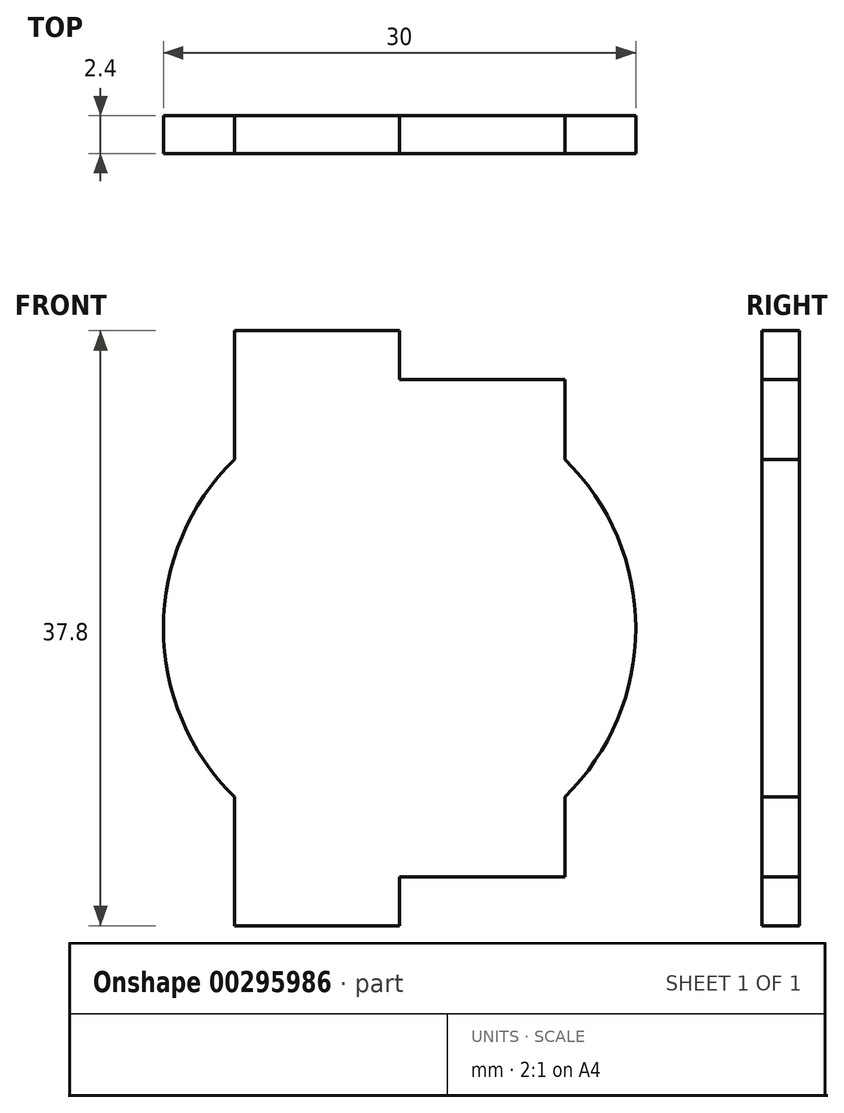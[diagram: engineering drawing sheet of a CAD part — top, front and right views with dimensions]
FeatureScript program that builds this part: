
annotation { "Feature Type Name" : "Feature", "Feature Type Description" : "" }
export const myFeature = defineFeature(function(context is Context, id is Id, definition is map)
    precondition{}
    {
        {
            var Q0;
            Q0=qCreatedBy(makeId("Front.planeOp"),FACE);
            var sketch = newSketch(context, id + "F0", { "sketchPlane" : qUnion([Q0])});
            skArc(sketch, "E0", {"start": v(-10.5, 10.71) * mm, "mid": v(-15, 0) * mm, "end": v(-10.5, -10.71) * mm});
            skLineSegment(sketch, "E1", {"start": v(-10.5, 10.71) * mm, "end": v(-10.5, 18.9) * mm});
            skLineSegment(sketch, "E2", {"start": v(-10.5, 18.9) * mm, "end": v(0, 18.9) * mm});
            skLineSegment(sketch, "E3", {"start": v(0, 18.9) * mm, "end": v(0, 15.8) * mm});
            skLineSegment(sketch, "E4", {"start": v(0, 15.8) * mm, "end": v(10.5, 15.8) * mm});
            skLineSegment(sketch, "E5", {"start": v(10.5, 15.8) * mm, "end": v(10.5, 10.71) * mm});
            skLineSegment(sketch, "E6", {"start": v(-10.5, -10.71) * mm, "end": v(-10.5, -18.9) * mm});
            skLineSegment(sketch, "E7", {"start": v(-10.5, -18.9) * mm, "end": v(0, -18.9) * mm});
            skLineSegment(sketch, "E8", {"start": v(0, -18.9) * mm, "end": v(0, -15.8) * mm});
            skLineSegment(sketch, "E9", {"start": v(0, -15.8) * mm, "end": v(10.5, -15.8) * mm});
            skLineSegment(sketch, "E10", {"start": v(10.5, -15.8) * mm, "end": v(10.5, -10.71) * mm});
            skArc(sketch, "E11.trimOffspring", {"start": v(10.5, -10.71) * mm, "mid": v(15, 0) * mm, "end": v(10.5, 10.71) * mm});
            skSolve(sketch);
        }
        {
            var Q0;
            Q0=makeQuery(id+"F0.imprint","IMPRINT",FACE,{"disambiguationData":[TD([[makeQuery(id+"F0.imprint","IMPRINT",EDGE,{"derivedFrom":sQuery(id+"F0.wireOp",EDGE,"E0")}),1.0]])]});
            extrude(context, id + "F1", {"entities" : qUnion([Q0]), "depth" : 2.4 * mm});
        }
    });
